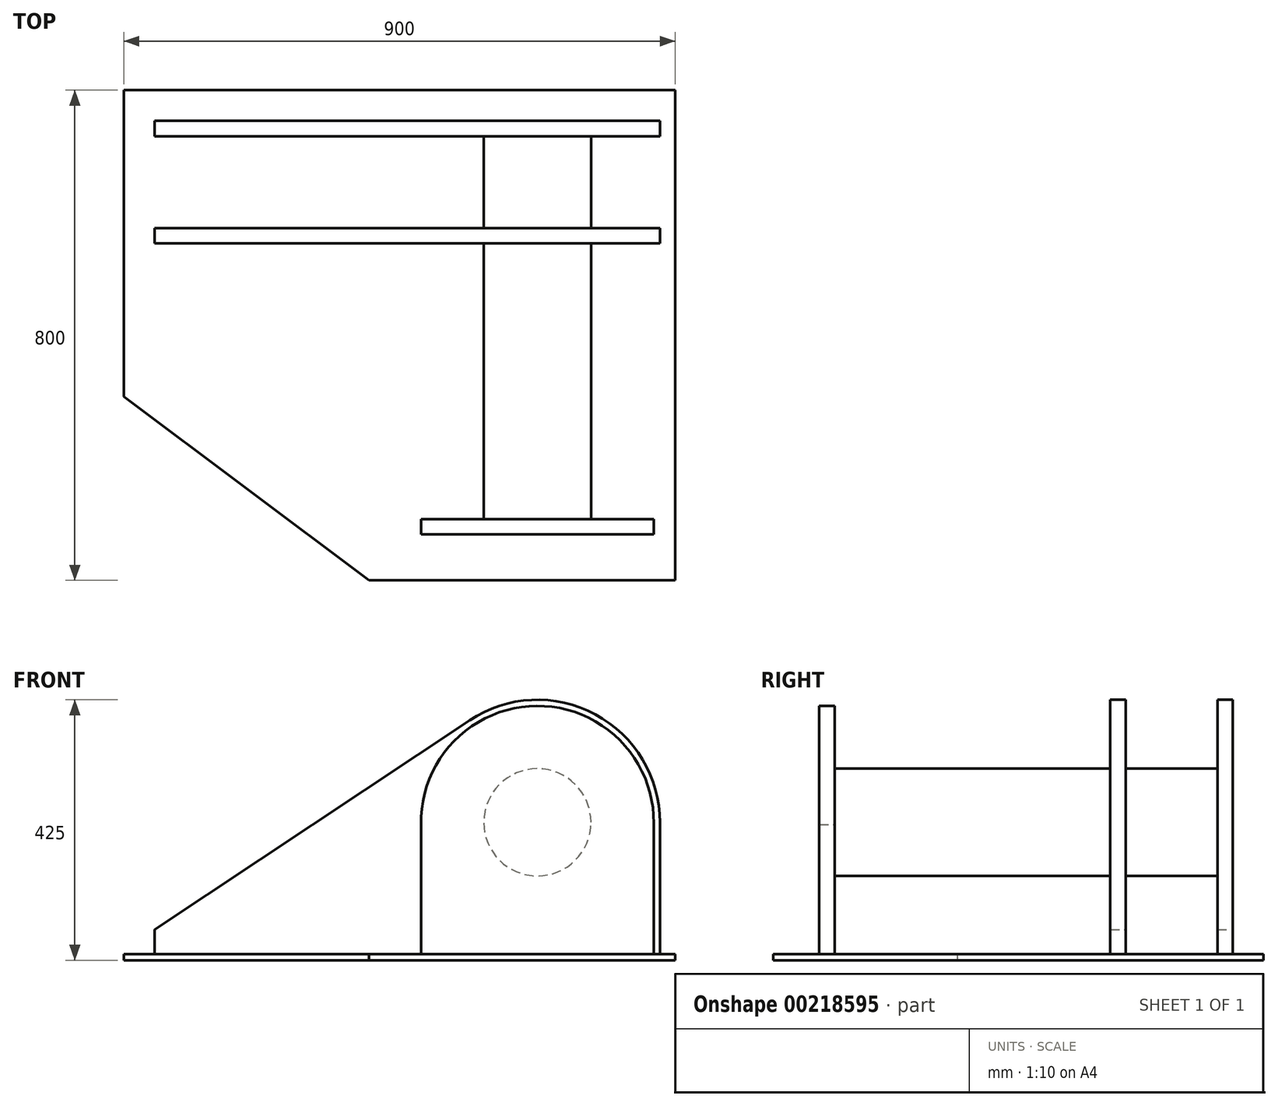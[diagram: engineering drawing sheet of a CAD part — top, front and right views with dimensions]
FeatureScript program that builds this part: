
annotation { "Feature Type Name" : "Feature", "Feature Type Description" : "" }
export const myFeature = defineFeature(function(context is Context, id is Id, definition is map)
    precondition{}
    {
        {
            var Q0;
            Q0=qCreatedBy(makeId("Top.planeOp"),FACE);
            var sketch = newSketch(context, id + "F0", { "sketchPlane" : qUnion([Q0])});
            skLineSegment(sketch, "E0", {"start": v(0, 0) * mm, "end": v(900, 0) * mm});
            skLineSegment(sketch, "E1", {"start": v(900, 0) * mm, "end": v(900, -800) * mm});
            skLineSegment(sketch, "E2", {"start": v(900, -800) * mm, "end": v(400, -800) * mm});
            skLineSegment(sketch, "E3", {"start": v(400, -800) * mm, "end": v(0, -500) * mm});
            skLineSegment(sketch, "E4", {"start": v(0, -500) * mm, "end": v(0, 0) * mm});
            skSolve(sketch);
        }
        {
            var Q0;
            Q0=qCreatedBy(makeId("Front.planeOp"),FACE);
            var sketch = newSketch(context, id + "F1", { "sketchPlane" : qUnion([Q0])});
            skLineSegment(sketch, "E5", {"start": v(50, 0) * mm, "end": v(50, 50) * mm});
            skArc(sketch, "E6", {"start": v(875, 225) * mm, "mid": v(769.53, 401.25) * mm, "end": v(564.35, 391.6) * mm});
            skLineSegment(sketch, "E7", {"start": v(50, 50) * mm, "end": v(564.35, 391.6) * mm});
            skLineSegment(sketch, "E8", {"start": v(875, 225) * mm, "end": v(875, 0) * mm});
            skLineSegment(sketch, "E9", {"start": v(50, 0) * mm, "end": v(875, 0) * mm});
            skSolve(sketch);
        }
        {
            var Q0;
            Q0=makeQuery(id+"F1.imprint","IMPRINT",FACE,{"disambiguationData":[TD([[makeQuery(id+"F1.imprint","IMPRINT",EDGE,{"derivedFrom":sQuery(id+"F1.wireOp",EDGE,"E5")}),-1.0]])]});
            cPlane(context, id + "F2", {"entities" : qUnion([Q0]), "cplaneType" : CPlaneType.OFFSET, "offset" : 700 * mm, "width" : 150 * mm, "height" : 150 * mm});
        }
        {
            var Q0;
            Q0=qCreatedBy(id+"F2.planeOp",FACE);
            var sketch = newSketch(context, id + "F3", { "sketchPlane" : qUnion([Q0])});
            skArc(sketch, "E10", {"start": v(865, 223.7) * mm, "mid": v(673.99, 415) * mm, "end": v(485.03, 221.68) * mm});
            skLineSegment(sketch, "E11", {"start": v(485.03, 221.68) * mm, "end": v(485.03, 0) * mm});
            skLineSegment(sketch, "E12", {"start": v(865, 223.7) * mm, "end": v(865, 0) * mm});
            skLineSegment(sketch, "E13", {"start": v(485.03, 0) * mm, "end": v(865, 0) * mm});
            skSolve(sketch);
        }
        {
            var Q0;
            Q0=makeQuery(id+"F0.imprint","IMPRINT",FACE,{"disambiguationData":[TD([[makeQuery(id+"F0.imprint","IMPRINT",EDGE,{"derivedFrom":sQuery(id+"F0.wireOp",EDGE,"E0")}),-1.0]])]});
            extrude(context, id + "F4", {"entities" : qUnion([Q0]), "depth" : 10 * mm});
        }
        {
            var Q0;
            Q0=makeQuery(id+"F1.imprint","IMPRINT",FACE,{"disambiguationData":[TD([[makeQuery(id+"F1.imprint","IMPRINT",EDGE,{"derivedFrom":sQuery(id+"F1.wireOp",EDGE,"E5")}),-1.0]])]});
            extrude(context, id + "F5", {"entities" : qUnion([Q0]), "depth" : 25 * mm});
        }
        {
            var Q0;
            Q0=makeQuery(id+"F5.opExtrude","SWEPT_BODY",BODY,{"disambiguationData":[OSD([sQuery(id+"F1.wireOp",EDGE,"E5"),sQuery(id+"F1.wireOp",EDGE,"E6"),sQuery(id+"F1.wireOp",EDGE,"E7"),sQuery(id+"F1.wireOp",EDGE,"E8"),sQuery(id+"F1.wireOp",EDGE,"E9")])]});
            var Q1;
            Q1=makeQuery(id+"F4.opExtrude","CAP_EDGE",EDGE,{"disambiguationData":[OSD([sQuery(id+"F0.wireOp",EDGE,"E4")])],"isStart":false});
            var Q2;
            Q2=makeQuery(id+"F4.opExtrude","CAP_EDGE",EDGE,{"disambiguationData":[OSD([sQuery(id+"F0.wireOp",EDGE,"E4")])],"isStart":false});
            transform(context, id + "F6", {"entities" : qUnion([Q0]), "transformType" : TransformType.TRANSLATION_DISTANCE, "transformDirection" : qUnion([Q2]), "distance" : 50 * mm, "oppositeDirection" : true, "makeCopy" : false});
        }
        {
            var Q0;
            Q0=makeQuery(id+"F5.opExtrude","SWEPT_BODY",BODY,{"disambiguationData":[OSD([sQuery(id+"F1.wireOp",EDGE,"E5"),sQuery(id+"F1.wireOp",EDGE,"E6"),sQuery(id+"F1.wireOp",EDGE,"E7"),sQuery(id+"F1.wireOp",EDGE,"E8"),sQuery(id+"F1.wireOp",EDGE,"E9")])]});
            var Q1;
            Q1=makeQuery(id+"F4.opExtrude","CAP_EDGE",EDGE,{"disambiguationData":[OSD([sQuery(id+"F0.wireOp",EDGE,"E4")])],"isStart":false});
            transform(context, id + "F7", {"entities" : qUnion([Q0]), "transformType" : TransformType.TRANSLATION_DISTANCE, "transformDirection" : qUnion([Q1]), "distance" : 175 * mm, "oppositeDirection" : true, "makeCopy" : true});
        }
        {
            var Q0;
            Q0=makeQuery(id+"F3.imprint","IMPRINT",FACE,{"disambiguationData":[TD([[makeQuery(id+"F3.imprint","IMPRINT",EDGE,{"derivedFrom":sQuery(id+"F3.wireOp",EDGE,"E10")}),1.0]])]});
            extrude(context, id + "F8", {"entities" : qUnion([Q0]), "operationType" : NewBodyOperationType.ADD, "depth" : 25 * mm});
        }
        {
            var Q0;
            Q0=qCreatedBy(id+"F2.planeOp",FACE);
            var sketch = newSketch(context, id + "F9", { "sketchPlane" : qUnion([Q0])});
            skCircle(sketch, "E14", {"center": v(675, 225) * mm, "radius": 87.5 * mm});
            skSolve(sketch);
        }
        {
            var Q0;
            Q0 = qSketchRegion(id + "F9", true);
            var Q1;
            Q1=makeQuery(id+"F5.opExtrude","CAP_FACE",FACE,{"disambiguationData":[OSD([sQuery(id+"F1.wireOp",EDGE,"E5"),sQuery(id+"F1.wireOp",EDGE,"E6"),sQuery(id+"F1.wireOp",EDGE,"E7"),sQuery(id+"F1.wireOp",EDGE,"E8"),sQuery(id+"F1.wireOp",EDGE,"E9")])],"isStart":false});
            extrude(context, id + "F10", {"entities" : qUnion([Q0]), "operationType" : NewBodyOperationType.ADD, "endBound" : BoundingType.UP_TO_SURFACE, "oppositeDirection" : true, "endBoundEntityFace" : qUnion([Q1]), "depth" : 25 * mm});
        }
    });
